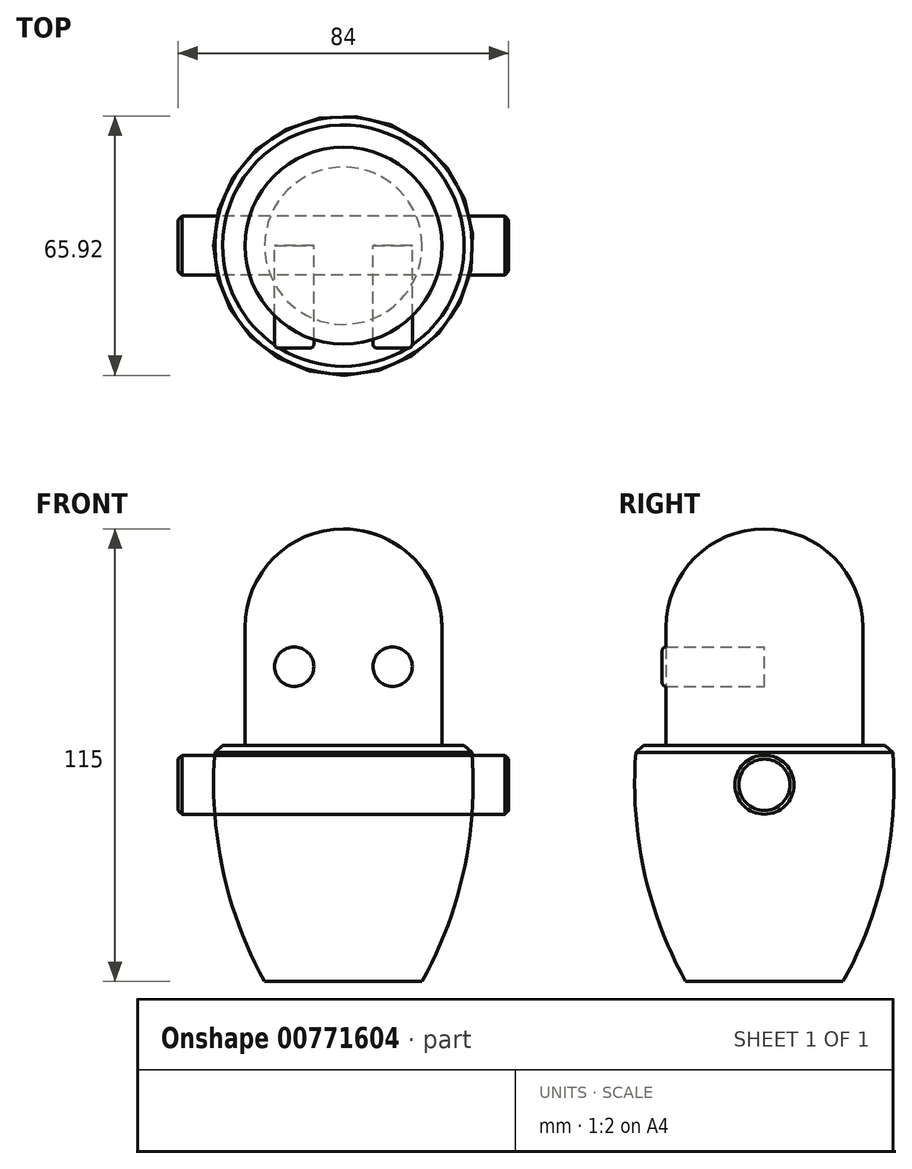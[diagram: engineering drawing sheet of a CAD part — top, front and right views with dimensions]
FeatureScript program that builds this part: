
annotation { "Feature Type Name" : "Feature", "Feature Type Description" : "" }
export const myFeature = defineFeature(function(context is Context, id is Id, definition is map)
    precondition{}
    {
        {
            var Q0;
            Q0=qCreatedBy(makeId("Front.planeOp"),FACE);
            var sketch = newSketch(context, id + "F0", { "sketchPlane" : qUnion([Q0])});
            skLineSegment(sketch, "E0", {"start": v(0, 0) * mm, "end": v(0, 60) * mm});
            skLineSegment(sketch, "E1", {"start": v(0, 60) * mm, "end": v(32.5, 60) * mm});
            skLineSegment(sketch, "E2", {"start": v(0, 0) * mm, "end": v(20, 0) * mm});
            skArc(sketch, "E3", {"start": v(20, 0) * mm, "mid": v(30.78, 29.06) * mm, "end": v(32.5, 60) * mm});
            skSolve(sketch);
        }
        {
            var Q0;
            Q0 = qSketchRegion(id + "F0", true);
            var Q1;
            Q1=sQuery(id+"F0.wireOp",EDGE,"E0");
            revolve(context, id + "F1", {"surfaceOperationType" : NewSurfaceOperationType.NEW, "entities" : qUnion([Q0]), "axis" : qUnion([Q1]), "revolveType" : RevolveType.FULL});
        }
        {
            var Q0;
            Q0=makeQuery(id+"F1.opRevolve","SWEPT_EDGE",EDGE,{"disambiguationData":[OSD([sQuery(id+"F0.wireOp",EDGE,"E1"),sQuery(id+"F0.wireOp",EDGE,"E3")])]});
            chamfer(context, id + "F2", {"entities" : qUnion([Q0]), "width" : 2 * mm, "tangentPropagation" : true});
        }
        {
            var Q0;
            Q0=makeQuery(id+"F1.opRevolve","SWEPT_FACE",FACE,{"disambiguationData":[OSD([sQuery(id+"F0.wireOp",EDGE,"E1")])]});
            var sketch = newSketch(context, id + "F3", { "sketchPlane" : qUnion([Q0])});
            skCircle(sketch, "E4", {"center": v(0, 0) * mm, "radius": 25 * mm});
            skSolve(sketch);
        }
        {
            var Q0;
            Q0=qCreatedBy(makeId("Front.planeOp"),FACE);
            var sketch = newSketch(context, id + "F4", { "sketchPlane" : qUnion([Q0])});
            skLineSegment(sketch, "E5", {"start": v(0, 0) * mm, "end": v(0, 90) * mm});
            skLineSegment(sketch, "E6", {"start": v(0, 90) * mm, "end": v(0, 80) * mm});
            skLineSegment(sketch, "E7", {"start": v(0, 80) * mm, "end": v(-12.5, 80) * mm});
            skLineSegment(sketch, "E8", {"start": v(-12.5, 80) * mm, "end": v(12.5, 80) * mm});
            skCircle(sketch, "E9", {"center": v(-12.5, 80) * mm, "radius": 5 * mm});
            skCircle(sketch, "E10", {"center": v(12.5, 80) * mm, "radius": 5 * mm});
            skSolve(sketch);
        }
        {
            var Q0;
            Q0 = qSketchRegion(id + "F3", true);
            extrude(context, id + "F5", {"entities" : qUnion([Q0]), "depth" : 55 * mm, "offsetDistance" : 25 * mm});
        }
        {
            var Q0;
            Q0=makeQuery(id+"F5.opExtrude","CAP_EDGE",EDGE,{"disambiguationData":[OSD([sQuery(id+"F3.wireOp",EDGE,"E4")])],"isStart":false});
            fillet(context, id + "F6", {"entities" : qUnion([Q0]), "radius" : 25 * mm, "tangentPropagation" : true, "allowEdgeOverflow" : false});
        }
        {
            var Q0;
            Q0 = qSketchRegion(id + "F4", true);
            extrude(context, id + "F7", {"entities" : qUnion([Q0]), "depth" : 26 * mm, "offsetDistance" : 25 * mm});
        }
        {
            var Q0;
            Q0=makeQuery(id+"F7.opExtrude","CAP_EDGE",EDGE,{"disambiguationData":[OSD([sQuery(id+"F4.wireOp",EDGE,"E9")])],"isStart":false});
            var Q1;
            Q1=makeQuery(id+"F7.opExtrude","CAP_EDGE",EDGE,{"disambiguationData":[OSD([sQuery(id+"F4.wireOp",EDGE,"E10")])],"isStart":false});
            fillet(context, id + "F8", {"entities" : qUnion([Q0, Q1]), "radius" : 1 * mm, "tangentPropagation" : true, "allowEdgeOverflow" : false});
        }
        {
            var Q0;
            Q0=qCreatedBy(makeId("Right.planeOp"),FACE);
            var sketch = newSketch(context, id + "F9", { "sketchPlane" : qUnion([Q0])});
            skLineSegment(sketch, "E11", {"start": v(0, 0) * mm, "end": v(0, 50) * mm});
            skCircle(sketch, "E12", {"center": v(0, 50) * mm, "radius": 7.5 * mm});
            skSolve(sketch);
        }
        {
            var Q0;
            Q0=makeQuery(id+"F9.imprint","IMPRINT",FACE,{"disambiguationData":[TD([[makeQuery(id+"F9.imprint","IMPRINT",EDGE,{"derivedFrom":sQuery(id+"F9.wireOp",EDGE,"E12")}),1.0]])]});
            extrude(context, id + "F10", {"entities" : qUnion([Q0]), "endBound" : BoundingType.SYMMETRIC, "depth" : 84 * mm, "offsetDistance" : 25 * mm});
        }
        {
            var Q0;
            Q0=makeQuery(id+"F10.opExtrude","CAP_EDGE",EDGE,{"disambiguationData":[OSD([sQuery(id+"F9.wireOp",EDGE,"E12")])],"isStart":false});
            var Q1;
            Q1=makeQuery(id+"F10.opExtrude","CAP_EDGE",EDGE,{"disambiguationData":[OSD([sQuery(id+"F9.wireOp",EDGE,"E12")])],"isStart":true});
            chamfer(context, id + "F11", {"entities" : qUnion([Q0, Q1]), "width" : 1 * mm, "tangentPropagation" : true});
        }
    });
